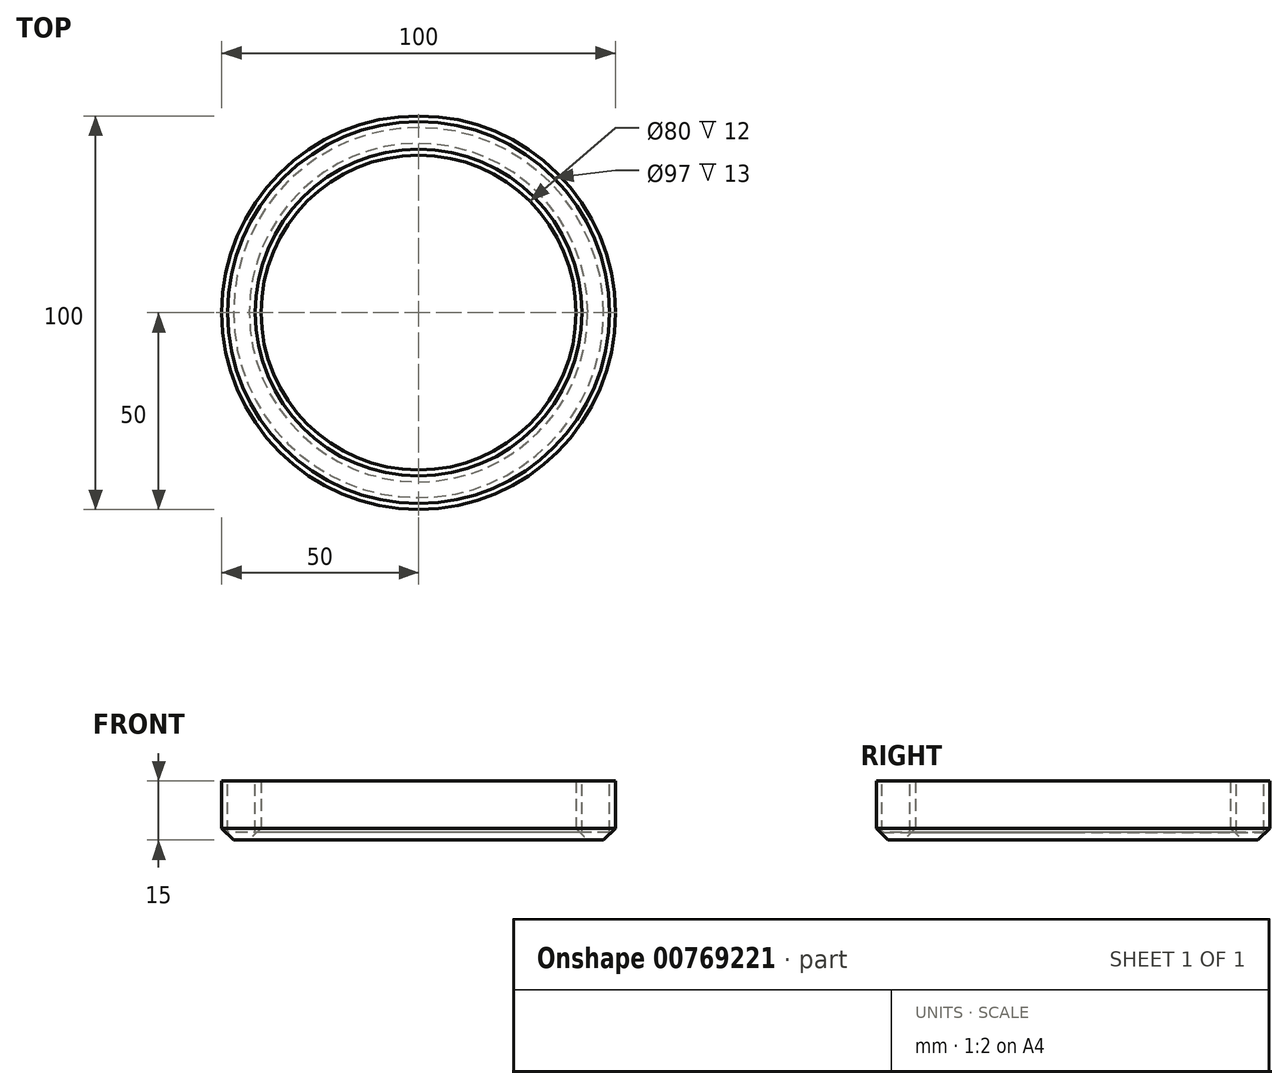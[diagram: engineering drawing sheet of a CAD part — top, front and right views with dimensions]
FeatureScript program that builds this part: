
annotation { "Feature Type Name" : "Feature", "Feature Type Description" : "" }
export const myFeature = defineFeature(function(context is Context, id is Id, definition is map)
    precondition{}
    {
        {
            var Q0;
            Q0=qCreatedBy(makeId("Top.planeOp"),FACE);
            var sketch = newSketch(context, id + "F0", { "sketchPlane" : qUnion([Q0])});
            skCircle(sketch, "E0", {"center": v(0, 0) * mm, "radius": 50 * mm});
            skCircle(sketch, "E1", {"center": v(0, 0) * mm, "radius": 40 * mm});
            skSolve(sketch);
        }
        {
            var Q0;
            Q0 = qSketchRegion(id + "F0", true);
            extrude(context, id + "F1", {"entities" : qUnion([Q0]), "depth" : 15 * mm, "offsetDistance" : 25 * mm});
        }
        {
            var Q0;
            Q0=makeQuery(id+"F1.opExtrude","CAP_FACE",FACE,{"disambiguationData":[OSD([sQuery(id+"F0.wireOp",EDGE,"E0"),sQuery(id+"F0.wireOp",EDGE,"E1")])],"isStart":false});
            var sketch = newSketch(context, id + "F2", { "sketchPlane" : qUnion([Q0])});
            skCircle(sketch, "E2", {"center": v(0, 0) * mm, "radius": 48.5 * mm});
            skCircle(sketch, "E3", {"center": v(0, 0) * mm, "radius": 41.5 * mm});
            skSolve(sketch);
        }
        {
            var Q0;
            Q0 = qSketchRegion(id + "F2", true);
            extrude(context, id + "F3", {"entities" : qUnion([Q0]), "operationType" : NewBodyOperationType.REMOVE, "oppositeDirection" : true, "depth" : 13 * mm, "offsetDistance" : 25 * mm});
        }
        {
            var Q0;
            Q0=makeQuery(id+"F1.opExtrude","CAP_EDGE",EDGE,{"disambiguationData":[OSD([sQuery(id+"F0.wireOp",EDGE,"E0")])],"isStart":true});
            chamfer(context, id + "F4", {"entities" : qUnion([Q0]), "width" : 3 * mm, "tangentPropagation" : true});
        }
        {
            var Q0;
            Q0=makeQuery(id+"F1.opExtrude","CAP_EDGE",EDGE,{"disambiguationData":[OSD([sQuery(id+"F0.wireOp",EDGE,"E1")])],"isStart":true});
            chamfer(context, id + "F5", {"entities" : qUnion([Q0]), "width" : 3 * mm, "tangentPropagation" : true});
        }
    });
